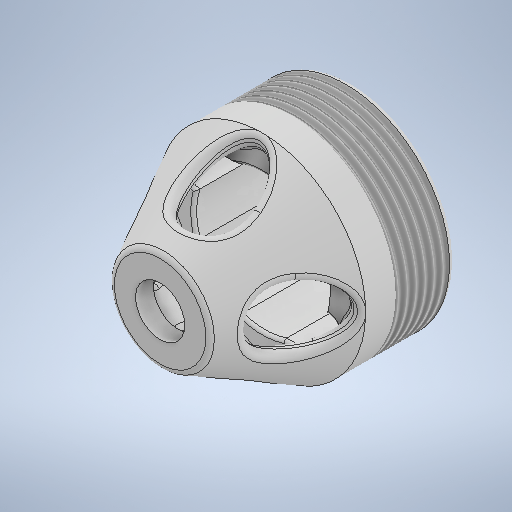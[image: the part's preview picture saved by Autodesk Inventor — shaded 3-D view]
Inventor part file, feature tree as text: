
AUTODESK INVENTOR PART (.ipt)
format: ipt  version: 2025.1 (Build 291241000, 241)  size: 813,568 bytes
history: native  units: mm
features: sketch x7, extrude x5, plane x3, fillet x2, revolve x1, pattern_circular x1, thread x1
ambient origin geometry x8: Origin, YZ Plane, XZ Plane, XY Plane, X Axis, Y Axis, Z Axis, Center Point
bodies: Body1 (feature_tree)
feature tree (20):
  revolve  "Umdrehung1"
  extrude  "Extrusion2"  Depth=2.5mm
  extrude  "Extrusion3"  Depth=30.0mm
  extrude  "Extrusion4"  Depth=8.2mm
  plane  "Arbeitsebene2"
  extrude  "Extrusion5"  Depth=15.0mm TaperAngle=0.0deg
  pattern_circular  "Runde Anordnung1"  [2 undecoded]
  plane  "Arbeitsebene3"
  extrude  "Extrusion6"  Depth=18.0mm TaperAngle=0.0deg
  sketch  "Skizze10"  dims[d20=18.0mm d21=0.0mm d22=22.8mm d23=18.0mm d24=0.0mm d26=0.0mm d27=6.0mm d28=5.0mm d29=7.5mm d30=18.0mm d31=0.0mm d32=40.0mm d33=360.0deg d35=5.5mm d36=5.5mm d37=4.0mm d38=4.0mm d39=18.0mm d40=0.0mm d41=18.0mm d42=14.0mm d43=17.0mm d54=10.0mm d55=0.0mm d56=1.0mm d57=0.5mm d58=34.6mm]
  plane  "Arbeitsebene4"
  thread  "Gewinde2"  [1 undecoded]
  fillet  "Rundung1"  Radius=6.0mm
  fillet  "Rundung2"  Radius=5.0mm
  sketch  "Skizze3"  dims[d4=3.0mm d5=2.5mm d6=2.5mm]
  sketch  "Skizze4"  dims[d8=15.0mm d12=30.0mm]
  sketch  "Skizze5"  dims[d13=14.0mm d14=8.2mm]
  sketch  "Skizze6"  dims[d15=90.0deg d16=15.0mm d17=0.0mm]
  sketch  "Skizze8"  dims[d18=21.6mm]
  sketch  "Skizze9"  dims[d19=21.6mm]
note: 3 required parameter values undecoded (feature->parameter linkage not recoverable at this tier; creation-order binding heuristic only, values carry confidence <= 0.55)
